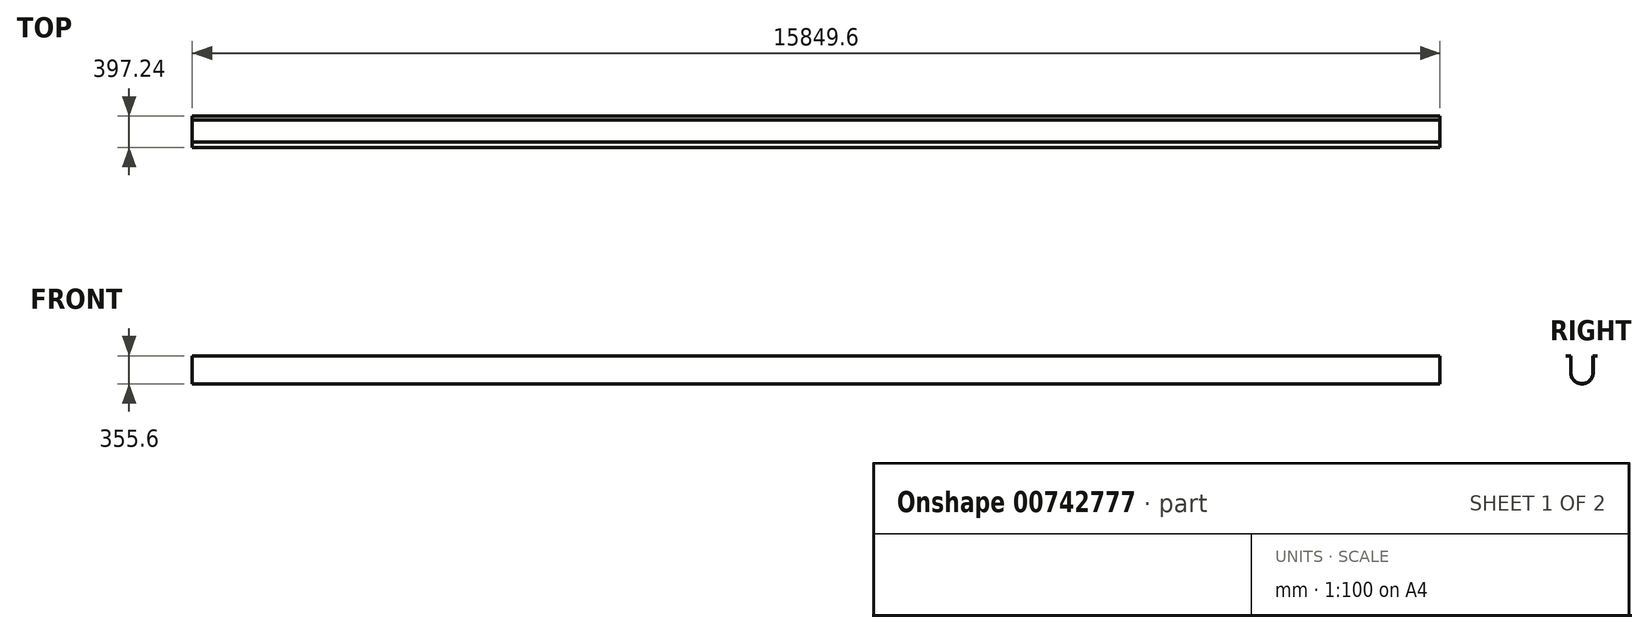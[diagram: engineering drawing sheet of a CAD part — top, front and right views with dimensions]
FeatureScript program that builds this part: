
annotation { "Feature Type Name" : "Feature", "Feature Type Description" : "" }
export const myFeature = defineFeature(function(context is Context, id is Id, definition is map)
    precondition{}
    {
        {
            var Q0;
            Q0=qCreatedBy(makeId("Right.planeOp"),FACE);
            var sketch = newSketch(context, id + "F0", { "sketchPlane" : qUnion([Q0])});
            skLineSegment(sketch, "E0.left", {"start": v(-147.58, 106.58) * mm, "end": v(-147.58, -102.97) * mm});
            skLineSegment(sketch, "E0.right", {"start": v(138.17, 106.58) * mm, "end": v(138.17, -102.97) * mm});
            skArc(sketch, "E1", {"start": v(-147.58, -102.97) * mm, "mid": v(-4.7, -245.85) * mm, "end": v(138.17, -102.97) * mm});
            skLineSegment(sketch, "E2.bottom", {"start": v(-208.33, 109.75) * mm, "end": v(-147.58, 109.75) * mm});
            skLineSegment(sketch, "E2.top", {"start": v(-208.33, 106.58) * mm, "end": v(-147.58, 106.58) * mm});
            skLineSegment(sketch, "E2.left", {"start": v(-208.33, 109.75) * mm, "end": v(-208.33, 106.58) * mm});
            skLineSegment(sketch, "E2.right", {"start": v(188.91, 109.75) * mm, "end": v(188.91, 106.58) * mm});
            skLineSegment(sketch, "E3.trimOffspring", {"start": v(138.17, 109.75) * mm, "end": v(188.91, 109.75) * mm});
            skLineSegment(sketch, "E4.trimOffspring", {"start": v(138.17, 106.58) * mm, "end": v(188.91, 106.58) * mm});
            skLineSegment(sketch, "E5.0", {"start": v(135, 109.75) * mm, "end": v(135, -102.97) * mm});
            skArc(sketch, "E5.1", {"start": v(-144.4, -102.97) * mm, "mid": v(-4.7, -242.67) * mm, "end": v(135, -102.97) * mm});
            skLineSegment(sketch, "E5.2", {"start": v(-144.4, 109.75) * mm, "end": v(-144.4, -102.97) * mm});
            skLineSegment(sketch, "E6", {"start": v(138.17, 109.75) * mm, "end": v(135, 109.75) * mm});
            skLineSegment(sketch, "E7", {"start": v(-144.4, 109.75) * mm, "end": v(-147.58, 109.75) * mm});
            skSolve(sketch);
        }
        {
            var Q0;
            Q0=makeQuery(id+"F0.imprint","IMPRINT",FACE,{"disambiguationData":[TD([[makeQuery(id+"F0.imprint","IMPRINT",EDGE,{"derivedFrom":sQuery(id+"F0.wireOp",EDGE,"E0.left")}),1.0]])]});
            extrude(context, id + "F1", {"entities" : qUnion([Q0]), "depth" : 15849.6 * mm, "offsetDistance" : 25.4 * mm});
        }
    });
